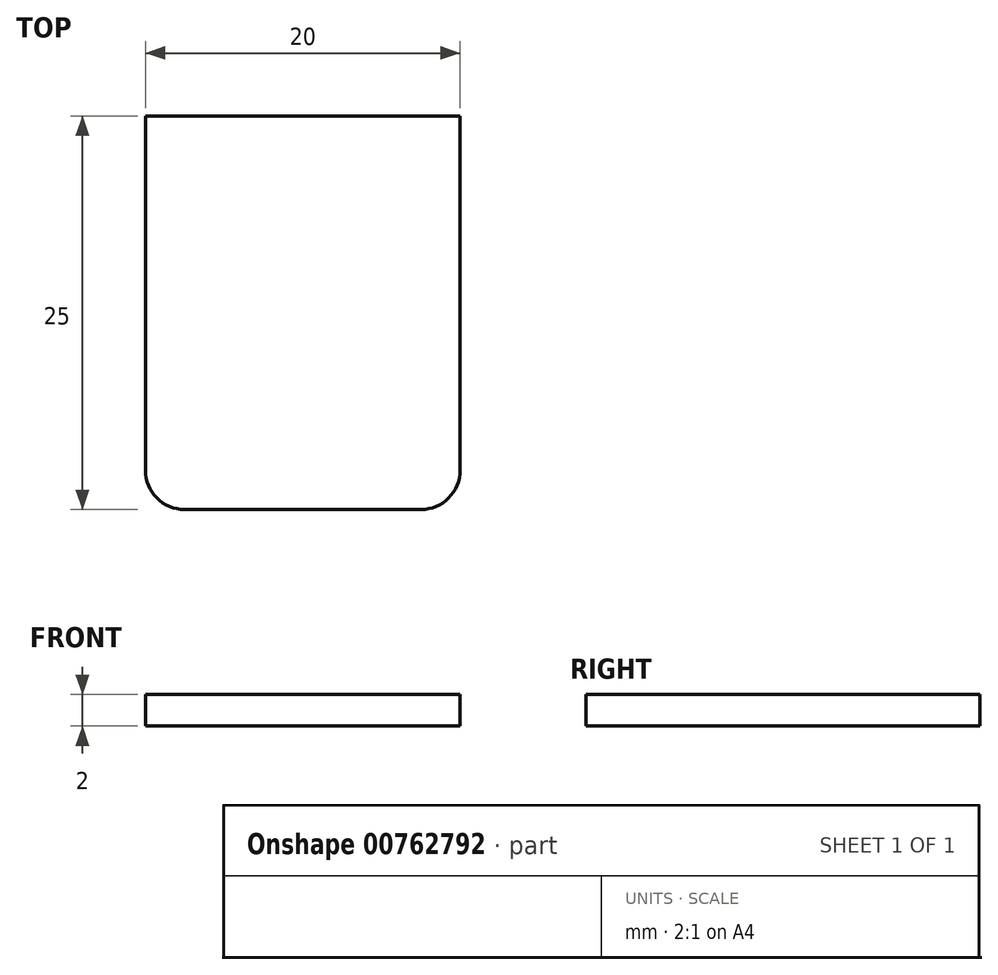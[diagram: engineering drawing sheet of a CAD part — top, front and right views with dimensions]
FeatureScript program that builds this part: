
annotation { "Feature Type Name" : "Feature", "Feature Type Description" : "" }
export const myFeature = defineFeature(function(context is Context, id is Id, definition is map)
    precondition{}
    {
        {
            var Q0;
            Q0=qCreatedBy(makeId("Top.planeOp"),FACE);
            var sketch = newSketch(context, id + "F0", { "sketchPlane" : qUnion([Q0])});
            skLineSegment(sketch, "E0.bottom", {"start": v(-10, 12.5) * mm, "end": v(10, 12.5) * mm});
            skLineSegment(sketch, "E0.top", {"start": v(-7.5, -12.5) * mm, "end": v(7.5, -12.5) * mm});
            skLineSegment(sketch, "E0.left", {"start": v(-10, 12.5) * mm, "end": v(-10, -10) * mm});
            skLineSegment(sketch, "E0.right", {"start": v(10, 12.5) * mm, "end": v(10, -10) * mm});
            skPoint(sketch, "E0.middle", {"position": v(0, 0) * mm});
            skPoint(sketch, "E1.visualSharp", {"position": v(-10, -12.5) * mm});
            skArc(sketch, "E1.filletArc", {"start": v(-10, -10) * mm, "mid": v(-9.27, -11.77) * mm, "end": v(-7.5, -12.5) * mm});
            skPoint(sketch, "E2.visualSharp", {"position": v(10, -12.5) * mm});
            skArc(sketch, "E2.filletArc", {"start": v(7.5, -12.5) * mm, "mid": v(9.27, -11.77) * mm, "end": v(10, -10) * mm});
            skSolve(sketch);
        }
        {
            var Q0;
            Q0=makeQuery(id+"F0.imprint","IMPRINT",FACE,{"disambiguationData":[TD([[makeQuery(id+"F0.imprint","IMPRINT",EDGE,{"derivedFrom":sQuery(id+"F0.wireOp",EDGE,"E0.bottom")}),-1.0]])]});
            extrude(context, id + "F1", {"entities" : qUnion([Q0]), "depth" : 2 * mm, "offsetDistance" : 25 * mm});
        }
    });
